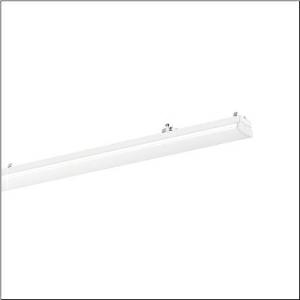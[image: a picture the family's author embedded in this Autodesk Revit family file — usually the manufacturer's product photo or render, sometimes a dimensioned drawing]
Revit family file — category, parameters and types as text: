
# Revit family: licross_11_recessed_opal_mo_51te1dcn485g
name_source: partatom
category: Lighting Fixtures
units: mm (PartAtom-declared; Revit-internal decimal feet)

## family parameters
Cut with Voids When Loaded = No
Host = Face
Light Source = No
Part Type = Normal
Room Calculation Point = No
Round Connector Dimension = Use Diameter
Shared = No

## types (1)
- --- (1 x LED, 8820 lm, 49.3 W, 4000K)
    Apparent Load = 49 VA
    CIE Flux Codes = 44 73 91 87 100
    Color Rendering = 80
    Color Temperature = 4000K
    Default Elevation = 1800 mm
    Description = Licross 11 recessed opal MO, luminaire insert, of sheet steel, coil coated, white, length: 1.500mm, width: 76mm, height: 87mm, LED rated luminous flux: 8.820lm, light colour: 840, SDCM (Standard Deviation of Colour Matching)MacAdam ≤ 2 SDCM (initial), control gear: ON/OFF Multilumen, CLOi, with plug, 3-pole, with phase selection, mains connection: 220..240V, AC, 50/60Hz, start of lifetime: 49W, end of service life: 55W, internal wiring halogen-free, primary optical cover: cover, of PMMA, light emission: direct with ceiling illumination distribution, primary light characteristic: symmetric, protection rating (complete): IP54, insulation class (complete): insulation class I (protective earthing), certification: CE, ENEC, VDE, UKCA, protection symbol: D if used in an environment with non-conductive dust loads with corresponding accessories, impact resistance: IK06, permissible ambient temperature for indoor applications: -35..+40°C, corresponds to IFS (International Featured Standards) requirements for safety and quality in the food industry, reducing of maximum allowable ambient temperature of 5°C with ceiling mounting, LABS conformity tested according to VDMA 24364:2018-05, The light source and the operating device comply with the requirements of the Ecodesign Regulation (EU) 2019/2020 and are replaceable in accordance with this regulation, packaging unit: 1 piece
    Height = 83 mm
    Lamp = 1 x LED
    Lamp Light Flux = 8820 lm
    Lamp Power = 49.3 W
    Lamp count = 1
    Length = 1500 mm
    Luminous efficacy = 179 lm/W
    Manufacturer = Siteco
    ModVariant = No
    Model = 51TE1DCN485G
    Mounting Place = Ceiling
    Mounting Type = Pendant
    Number of Poles = 1
    OnlyDefault = Yes
    Power Factor = 1
    Product Name = Licross 11 recessed opal MO
    Product group = luminaire insert | ceiling pendant
    ProductGroupID = 901
    Protection Class = Protection class I
    Protection Degree = IP 54
    RLX_Detail_Level = 1
    RLX_Emergency_Light_Flux = 0 lm
    RLX_Emergency_Type = 0
    RLX_Emergency_Type_DB = No
    RlxData = <blob elided: 24833 chars, md5=4774d859>
    Socket = socket
    Standby Power = 0 W
    System Light Flux = 8820 lm
    System Power = 49 W
    Type Comments = factory setting: luminous flux: 100 % | (A | C | E) | 113 mA
    Type Image = l_1313666.jpg
    URL = http://relux.com
    VarID = @adj_000177
    Voltage = 0 V
    Weight = 0.00 kg
    Width = 76 mm

## geometry (parser evidence)
native form markers: Blend x4, Sweep x14
no freeform markers — native parametric forms only
